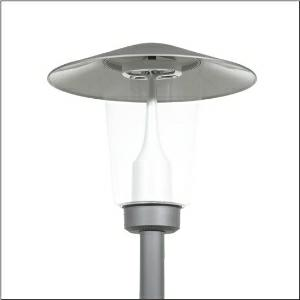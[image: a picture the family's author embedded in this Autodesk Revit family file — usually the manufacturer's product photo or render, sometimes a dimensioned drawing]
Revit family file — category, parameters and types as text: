
# Revit family: pilzleuchte_iq___st1_2a_5xa5235mf14h_7035
name_source: partatom
category: Lighting Fixtures
units: mm (PartAtom-declared; Revit-internal decimal feet)

## family parameters
Cut with Voids When Loaded = No
Host = Face
Light Source = No
Part Type = Normal
Room Calculation Point = No
Round Connector Dimension = Use Diameter
Shared = No

## types (1)
- --- (1 x LED, 1550 lm, 11.8 W, 2700K)
    Apparent Load = 12 VA
    CIE Flux Codes = 24 61 93 98 100
    Color Rendering = 70
    Color Temperature = 2700K
    Default Elevation = 1800 mm
    Description = Mushroom Luminaire iQ, mast luminaire, Module 540 iQ-SR, primary light control with 3 zone facetted reflector, of plastic, silver coated, highly specular, structured, primary optical cover: cover, of PMMA, transparent, light distribution: ST1.2a, light emission: direct distribution, primary light characteristic: asymmetric, installation type: post-top, LED, High Power LED, rated luminous flux: 1.550lm, luminous efficacy: 131lm/W, light colour: 727, colour temperature: 2700K, control gear: ECG iQ, control: presetting dimming logarithmic, Street-Remote, Auto-Match, Temp-Guard, Lumen-Switch, Night-Set, Smart-Wire, Light-Fading, Desk-Remote (wireless, voltage-free reading and setting of iQ features in the workshop via application-optimized NFC function/RFID function), optimised constant luminous flux control (CLO 2.0), with terminal, 6-pole, max. 2.5mm², mains connection: 220..240V, AC, 50/60Hz, start of lifetime: 12W, end of lifetime: 12W, reduction: 6W, luminaire housing, upper part, of glass-fibre reinforced polyester, coated, Siteco® metallic grey (DB 702S), diameter: 650mm, height: 586mm, spigot size: d x l = 76 x 70mm (post-top) | with reducer (optional accessory) 60 x 70mm, post-top mast mounting element, of diecast aluminium, coated, Siteco® metallic grey (DB 702S), Module 540 iQ-SR, traffic white (RAL 9016), equipment: standard, protection rating (complete): IP65, insulation class (complete): insulation class II (safety insulation), certification: CE, ENEC, VDE, packaging unit: 1 piece

Light Distribution: ST1.2a
    Height = 586 mm
    Lamp = 1 x LED
    Lamp Light Flux = 1550 lm
    Lamp Power = 11.8 W
    Lamp count = 1
    Length = 650 mm
    Luminous efficacy = 131 lm/W
    Manufacturer = Siteco
    ModVariant = No
    Model = 5XA5235MF14H
    Number of Poles = 1
    OnlyDefault = Yes
    Power Factor = 1
    Product Name = Pilzleuchte iQ | ST1.2a
    Product group = mast luminaire | pylon top
    ProductGroupID = 6100
    Protection Class = Protection class II
    Protection Degree = IP 65
    RLX_Detail_Level = 1
    RlxData = <blob elided: 123497 chars, md5=f1bb1526>
    Socket = socket
    Standby Power = 0 W
    System Light Flux = 1550 lm
    System Power = 12 W
    Type Comments = factory setting: luminous flux: 100 % | dim-lin: 254 | 472 mA
    Type Image = l_1006077.jpg
    URL = http://relux.com
    VarID = @adj_063281
    Voltage = 0 V
    Weight = 0.00 kg
    Width = 0 mm  [stored 0 ft]

note: [stored X ft] marks values corroborated as IEEE doubles in the binary element streams (Revit-internal decimal feet)

## geometry (parser evidence)
native form markers: Blend x4, Sweep x12
no freeform markers — native parametric forms only
